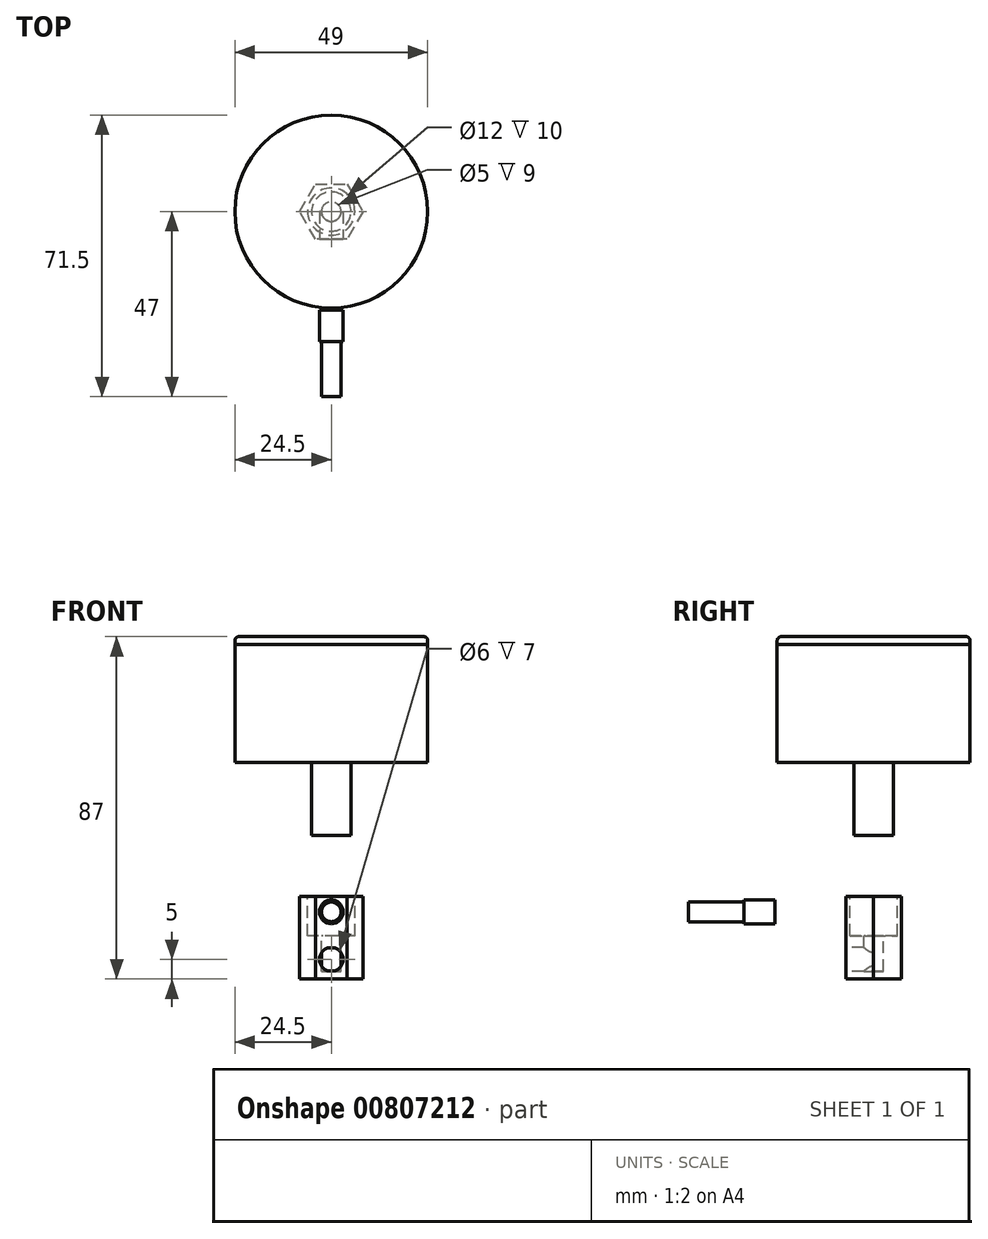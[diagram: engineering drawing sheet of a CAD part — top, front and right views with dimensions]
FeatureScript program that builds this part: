
annotation { "Feature Type Name" : "Feature", "Feature Type Description" : "" }
export const myFeature = defineFeature(function(context is Context, id is Id, definition is map)
    precondition{}
    {
        {
            var Q0;
            Q0=qCreatedBy(makeId("Top.planeOp"),FACE);
            var sketch = newSketch(context, id + "F0", { "sketchPlane" : qUnion([Q0])});
            skCircle(sketch, "E0", {"center": v(0, 0) * mm, "radius": 24.5 * mm});
            skSolve(sketch);
        }
        {
            var Q0;
            Q0 = qSketchRegion(id + "F0", true);
            extrude(context, id + "F1", {"entities" : qUnion([Q0]), "depth" : 30 * mm, "offsetDistance" : 25 * mm});
        }
        {
            var Q0;
            Q0=makeQuery(id+"F1.opExtrude","CAP_FACE",FACE,{"disambiguationData":[OSD([sQuery(id+"F0.wireOp",EDGE,"E0")])],"isStart":true});
            var sketch = newSketch(context, id + "F2", { "sketchPlane" : qUnion([Q0])});
            skCircle(sketch, "E1", {"center": v(0, 0) * mm, "radius": 5 * mm});
            skSolve(sketch);
        }
        {
            var Q0;
            Q0 = qSketchRegion(id + "F2", true);
            extrude(context, id + "F3", {"entities" : qUnion([Q0]), "depth" : (48.5 - 30) * mm, "offsetDistance" : 25 * mm});
        }
        {
            var Q0;
            Q0=qCreatedBy(makeId("Top.planeOp"),FACE);
            cPlane(context, id + "F4", {"entities" : qUnion([Q0]), "cplaneType" : CPlaneType.OFFSET, "offset" : 55 * mm, "oppositeDirection" : true, "width" : 150 * mm, "height" : 150 * mm});
        }
        {
            var Q0;
            Q0=qCreatedBy(id+"F4.planeOp",FACE);
            var sketch = newSketch(context, id + "F5", { "sketchPlane" : qUnion([Q0])});
            skCircle(sketch, "E2.cCircle", {"center": v(0, 0) * mm, "radius": 7 * mm, "construction": true});
            skLineSegment(sketch, "E2.0", {"start": v(-4.04, 7) * mm, "end": v(4.04, 7) * mm});
            skLineSegment(sketch, "E2.1", {"start": v(4.04, 7) * mm, "end": v(8.08, 0) * mm});
            skLineSegment(sketch, "E2.2", {"start": v(8.08, 0) * mm, "end": v(4.04, -7) * mm});
            skLineSegment(sketch, "E2.3", {"start": v(4.04, -7) * mm, "end": v(-4.04, -7) * mm});
            skLineSegment(sketch, "E2.4", {"start": v(-4.04, -7) * mm, "end": v(-8.08, 0) * mm});
            skLineSegment(sketch, "E2.5", {"start": v(-8.08, 0) * mm, "end": v(-4.04, 7) * mm});
            skPoint(sketch, "E2.0.midPoint", {"position": v(0, 7) * mm});
            skSolve(sketch);
        }
        {
            var Q0;
            Q0 = qSketchRegion(id + "F5", true);
            extrude(context, id + "F6", {"entities" : qUnion([Q0]), "depth" : 21 * mm, "offsetDistance" : 25 * mm});
        }
        {
            var Q0;
            Q0=makeQuery(id+"F6.opExtrude","CAP_FACE",FACE,{"disambiguationData":[OSD([sQuery(id+"F5.wireOp",EDGE,"E2.0"),sQuery(id+"F5.wireOp",EDGE,"E2.1"),sQuery(id+"F5.wireOp",EDGE,"E2.2"),sQuery(id+"F5.wireOp",EDGE,"E2.3"),sQuery(id+"F5.wireOp",EDGE,"E2.4"),sQuery(id+"F5.wireOp",EDGE,"E2.5")])],"isStart":false});
            var sketch = newSketch(context, id + "F7", { "sketchPlane" : qUnion([Q0])});
            skCircle(sketch, "E3", {"center": v(0, 0) * mm, "radius": 6 * mm});
            skSolve(sketch);
        }
        {
            var Q0;
            Q0 = qSketchRegion(id + "F7", true);
            extrude(context, id + "F8", {"entities" : qUnion([Q0]), "operationType" : NewBodyOperationType.REMOVE, "oppositeDirection" : true, "depth" : 10 * mm, "offsetDistance" : 25 * mm});
        }
        {
            var Q0;
            Q0=makeQuery(id+"F8.boolean.opBoolean","COPY",FACE,{"derivedFrom":makeQuery(id+"F8.opExtrude","CAP_FACE",FACE,{"disambiguationData":[OSD([sQuery(id+"F7.wireOp",EDGE,"E3")])],"isStart":false})});
            var sketch = newSketch(context, id + "F9", { "sketchPlane" : qUnion([Q0])});
            skCircle(sketch, "E4", {"center": v(0, 0) * mm, "radius": 2.5 * mm});
            skSolve(sketch);
        }
        {
            var Q0;
            Q0 = qSketchRegion(id + "F9", true);
            extrude(context, id + "F10", {"entities" : qUnion([Q0]), "operationType" : NewBodyOperationType.REMOVE, "oppositeDirection" : true, "depth" : 9 * mm, "offsetDistance" : 25 * mm});
        }
        {
            var Q0;
            Q0=makeQuery(id+"F6.opExtrude","SWEPT_FACE",FACE,{"disambiguationData":[OSD([sQuery(id+"F5.wireOp",EDGE,"E2.3")])]});
            var sketch = newSketch(context, id + "F11", { "sketchPlane" : qUnion([Q0])});
            skCircle(sketch, "E5", {"center": v(0, -50) * mm, "radius": 3 * mm});
            skSolve(sketch);
        }
        {
            var Q0;
            Q0 = qSketchRegion(id + "F11", true);
            var Q1;
            Q1=makeQuery(id+"F10.boolean.opBoolean","COPY",FACE,{"derivedFrom":makeQuery(id+"F10.opExtrude","SWEPT_FACE",FACE,{"disambiguationData":[OSD([sQuery(id+"F9.wireOp",EDGE,"E4")])]})});
            extrude(context, id + "F12", {"entities" : qUnion([Q0]), "operationType" : NewBodyOperationType.REMOVE, "oppositeDirection" : true, "depth" : 7 * mm, "endBoundEntityFace" : qUnion([Q1]), "offsetDistance" : 25 * mm});
        }
        {
            var Q0;
            Q0=qCreatedBy(makeId("Front.planeOp"),FACE);
            cPlane(context, id + "F13", {"entities" : qUnion([Q0]), "cplaneType" : CPlaneType.OFFSET, "offset" : 25 * mm, "width" : 150 * mm, "height" : 150 * mm});
        }
        {
            var Q0;
            Q0=qCreatedBy(id+"F13.planeOp",FACE);
            var sketch = newSketch(context, id + "F14", { "sketchPlane" : qUnion([Q0])});
            skCircle(sketch, "E6", {"center": v(0, -37.92) * mm, "radius": 3 * mm});
            skSolve(sketch);
        }
        {
            var Q0;
            Q0 = qSketchRegion(id + "F14", true);
            extrude(context, id + "F15", {"entities" : qUnion([Q0]), "depth" : (22 - 14) * mm, "offsetDistance" : 25 * mm});
        }
        {
            var Q0;
            Q0=makeQuery(id+"F15.opExtrude","CAP_FACE",FACE,{"disambiguationData":[OSD([sQuery(id+"F14.wireOp",EDGE,"E6")])],"isStart":false});
            var sketch = newSketch(context, id + "F16", { "sketchPlane" : qUnion([Q0])});
            skCircle(sketch, "E7", {"center": v(0, -37.92) * mm, "radius": 2.5 * mm});
            skSolve(sketch);
        }
        {
            var Q0;
            Q0 = qSketchRegion(id + "F16", true);
            extrude(context, id + "F17", {"entities" : qUnion([Q0]), "operationType" : NewBodyOperationType.ADD, "depth" : 14 * mm, "offsetDistance" : 25 * mm});
        }
        {
            var Q0;
            Q0=makeQuery(id+"F1.opExtrude","CAP_FACE",FACE,{"disambiguationData":[OSD([sQuery(id+"F0.wireOp",EDGE,"E0")])],"isStart":false});
            var sketch = newSketch(context, id + "F18", { "sketchPlane" : qUnion([Q0])});
            skCircle(sketch, "E8", {"center": v(0, 0) * mm, "radius": 24.5 * mm});
            skSolve(sketch);
        }
        {
            var Q0;
            Q0 = qSketchRegion(id + "F18", true);
            extrude(context, id + "F19", {"entities" : qUnion([Q0]), "depth" : 2 * mm, "offsetDistance" : 25 * mm});
        }
        {
            var Q0;
            Q0=makeQuery(id+"F19.opExtrude","CAP_EDGE",EDGE,{"disambiguationData":[OSD([sQuery(id+"F18.wireOp",EDGE,"E8")])],"isStart":false});
            fillet(context, id + "F20", {"entities" : qUnion([Q0]), "radius" : 1 * mm, "tangentPropagation" : true, "allowEdgeOverflow" : false});
        }
    });
